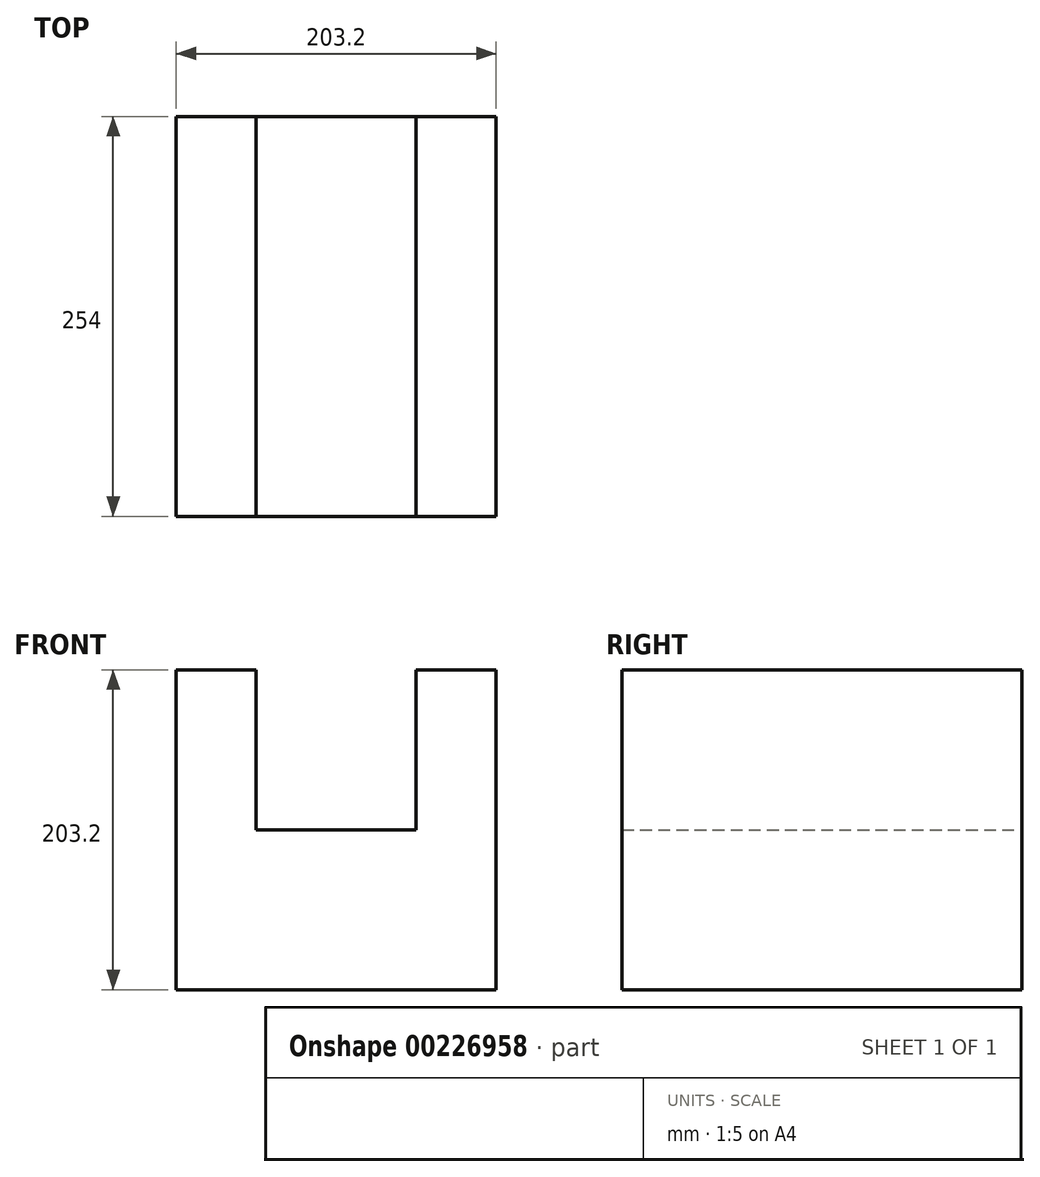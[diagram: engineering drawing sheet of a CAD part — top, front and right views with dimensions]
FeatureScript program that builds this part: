
annotation { "Feature Type Name" : "Feature", "Feature Type Description" : "" }
export const myFeature = defineFeature(function(context is Context, id is Id, definition is map)
    precondition{}
    {
        {
            var Q0;
            Q0=qCreatedBy(makeId("Front.planeOp"),FACE);
            var sketch = newSketch(context, id + "F0", { "sketchPlane" : qUnion([Q0])});
            skLineSegment(sketch, "E0.top", {"start": v(-100.8, -101.6) * mm, "end": v(102.4, -101.6) * mm});
            skLineSegment(sketch, "E0.left", {"start": v(-100.8, 101.6) * mm, "end": v(-100.8, -101.6) * mm});
            skLineSegment(sketch, "E0.right", {"start": v(102.4, 101.6) * mm, "end": v(102.4, -101.6) * mm});
            skLineSegment(sketch, "E1", {"start": v(-100.8, 101.6) * mm, "end": v(-50, 101.6) * mm});
            skLineSegment(sketch, "E2", {"start": v(51.6, 101.6) * mm, "end": v(102.4, 101.6) * mm});
            skLineSegment(sketch, "E3", {"start": v(-50, 101.6) * mm, "end": v(-50, 0) * mm});
            skLineSegment(sketch, "E4", {"start": v(51.6, 101.6) * mm, "end": v(51.6, 0) * mm});
            skLineSegment(sketch, "E5", {"start": v(51.6, 0) * mm, "end": v(-50, 0) * mm});
            skSolve(sketch);
        }
        {
            var Q0;
            Q0=makeQuery(id+"F0.imprint","IMPRINT",FACE,{"disambiguationData":[TD([[makeQuery(id+"F0.imprint","IMPRINT",EDGE,{"derivedFrom":sQuery(id+"F0.wireOp",EDGE,"E0.top")}),1.0]])]});
            extrude(context, id + "F1", {"entities" : qUnion([Q0]), "depth" : 254 * mm});
        }
    });
